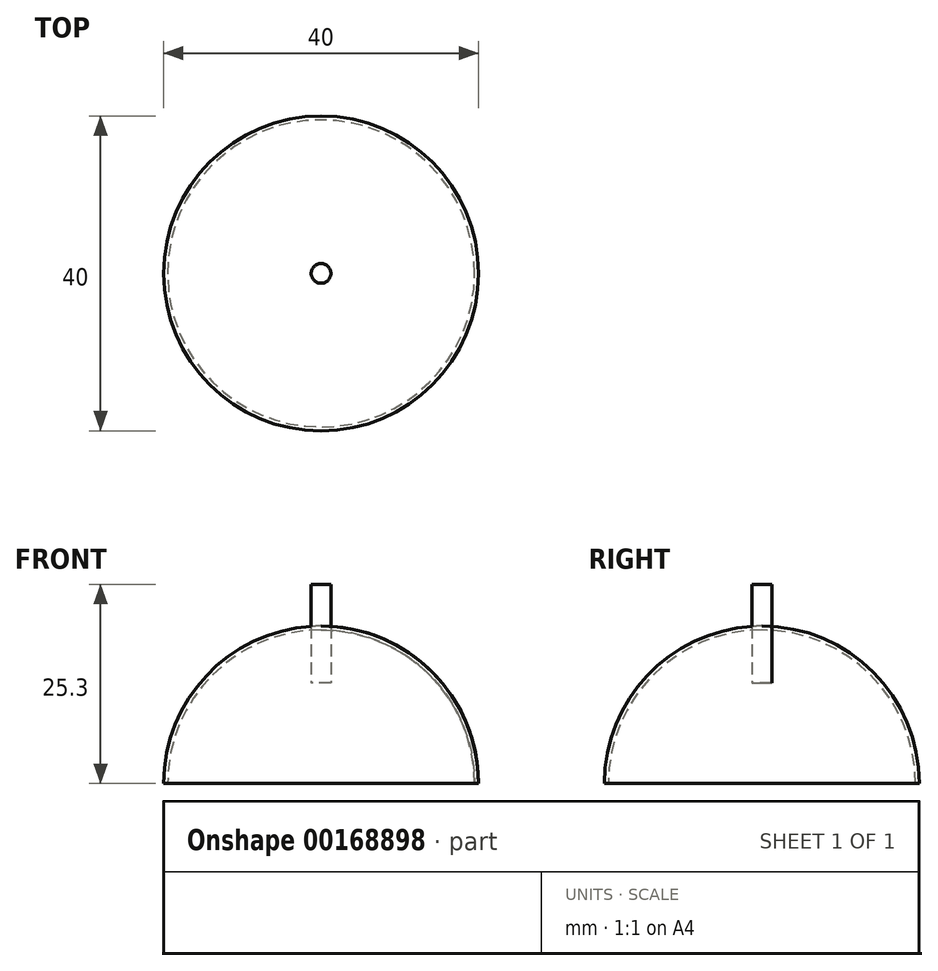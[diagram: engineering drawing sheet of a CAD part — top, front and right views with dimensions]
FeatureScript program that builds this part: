
annotation { "Feature Type Name" : "Feature", "Feature Type Description" : "" }
export const myFeature = defineFeature(function(context is Context, id is Id, definition is map)
    precondition{}
    {
        {
            var Q0;
            Q0=qCreatedBy(makeId("Front.planeOp"),FACE);
            var sketch = newSketch(context, id + "F0", { "sketchPlane" : qUnion([Q0])});
            skLineSegment(sketch, "E0", {"start": v(0, 0) * mm, "end": v(0, 20) * mm});
            skArc(sketch, "E1", {"start": v(0, 20) * mm, "mid": v(14.14, 14.14) * mm, "end": v(20, 0) * mm});
            skLineSegment(sketch, "E2", {"start": v(20, 0) * mm, "end": v(0, 0) * mm});
            skSolve(sketch);
        }
        {
            var Q0;
            Q0=makeQuery(id+"F0.imprint","IMPRINT",FACE,{"disambiguationData":[TD([[makeQuery(id+"F0.imprint","IMPRINT",EDGE,{"derivedFrom":sQuery(id+"F0.wireOp",EDGE,"E0")}),-1.0]])]});
            var Q1;
            Q1=sQuery(id+"F0.wireOp",EDGE,"E0");
            revolve(context, id + "F1", {"entities" : qUnion([Q0]), "axis" : qUnion([Q1]), "revolveType" : RevolveType.FULL});
        }
        {
            var Q0;
            Q0=makeQuery(id+"F1.opRevolve","SWEPT_FACE",FACE,{"disambiguationData":[OSD([sQuery(id+"F0.wireOp",EDGE,"E2")])]});
            shell(context, id + "F2", {"entities" : qUnion([Q0]), "thickness" : .5 * mm});
        }
        {
            var Q0;
            Q0=qCreatedBy(makeId("Top.planeOp"),FACE);
            cPlane(context, id + "F3", {"entities" : qUnion([Q0]), "cplaneType" : CPlaneType.OFFSET, "offset" : 12.8 * mm, "width" : 150 * mm, "height" : 150 * mm});
        }
        {
            var Q0;
            Q0=qCreatedBy(id+"F3.planeOp",FACE);
            var sketch = newSketch(context, id + "F4", { "sketchPlane" : qUnion([Q0])});
            skCircle(sketch, "E3", {"center": v(0, 0) * mm, "radius": 1.25 * mm});
            skSolve(sketch);
        }
        {
            var Q0;
            Q0=makeQuery(id+"F4.imprint","IMPRINT",FACE,{"disambiguationData":[TD([[makeQuery(id+"F4.imprint","IMPRINT",EDGE,{"derivedFrom":sQuery(id+"F4.wireOp",EDGE,"E3")}),1.0]])]});
            extrude(context, id + "F5", {"entities" : qUnion([Q0]), "depth" : 12.5 * mm});
        }
    });
